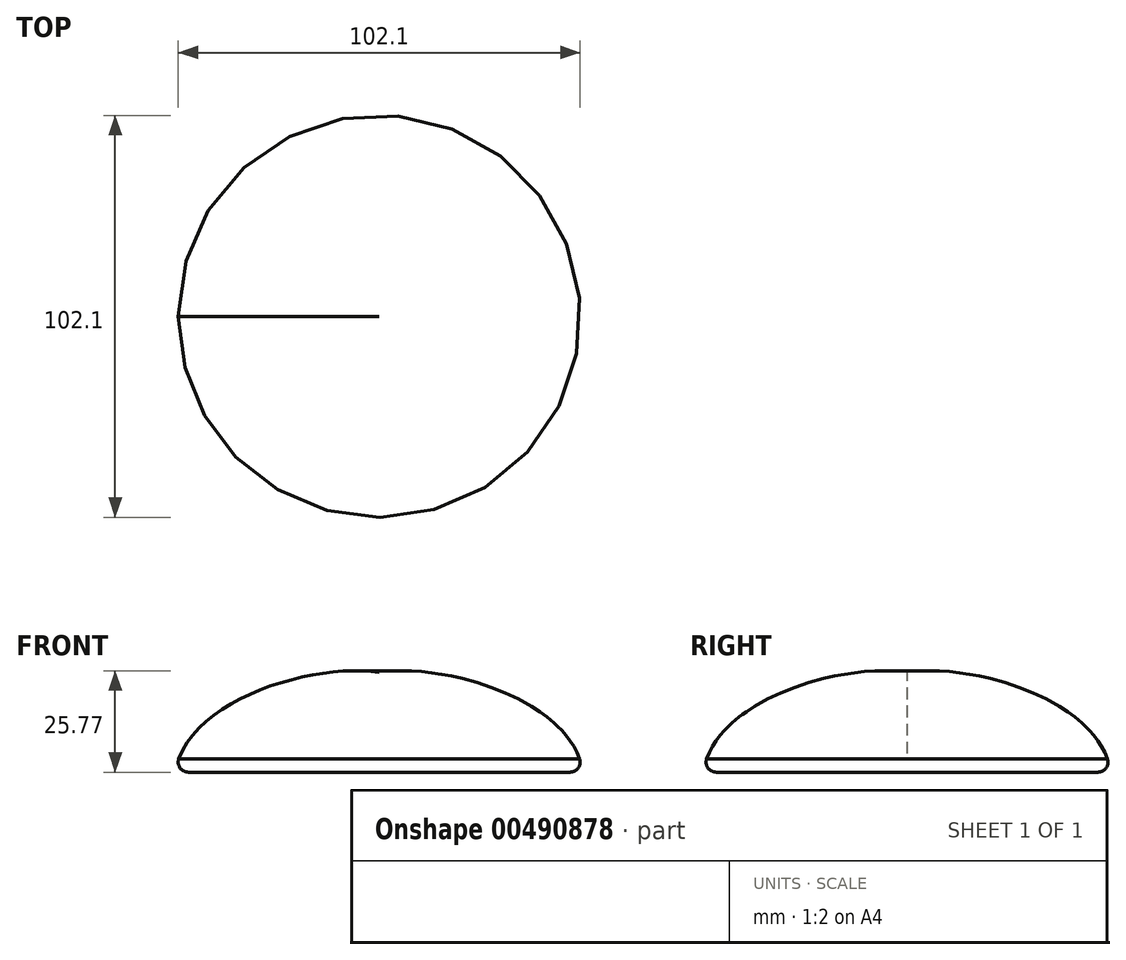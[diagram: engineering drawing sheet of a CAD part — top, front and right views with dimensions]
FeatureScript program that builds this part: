
annotation { "Feature Type Name" : "Feature", "Feature Type Description" : "" }
export const myFeature = defineFeature(function(context is Context, id is Id, definition is map)
    precondition{}
    {
        {
            var Q0;
            Q0=qCreatedBy(makeId("Front.planeOp"),FACE);
            var sketch = newSketch(context, id + "F0", { "sketchPlane" : qUnion([Q0])});
            skLineSegment(sketch, "E0", {"start": v(0, 25.4) * mm, "end": v(0, 0) * mm});
            skFitSpline(sketch, "E1", {"points": [v(0, 25.4) * mm, v(-51.8, 0) * mm], "startDerivative": vector(-49.56, 7.13) * mm, "endDerivative": vector(-8.85, -56.04) * mm});
            skLineSegment(sketch, "E2", {"start": v(-51.8, 0) * mm, "end": v(0, 0) * mm});
            skSolve(sketch);
        }
        {
            var Q0;
            Q0=makeQuery(id+"F0.imprint","IMPRINT",FACE,{"disambiguationData":[TD([[makeQuery(id+"F0.imprint","IMPRINT",EDGE,{"derivedFrom":sQuery(id+"F0.wireOp",EDGE,"E0")}),-1.0]])]});
            var Q1;
            Q1=sQuery(id+"F0.wireOp",EDGE,"E0");
            revolve(context, id + "F1", {"entities" : qUnion([Q0]), "axis" : qUnion([Q1]), "revolveType" : RevolveType.FULL});
        }
        {
            var Q0;
            Q0=makeQuery(id+"F1.opRevolve","SWEPT_FACE",FACE,{"disambiguationData":[OSD([sQuery(id+"F0.wireOp",EDGE,"E1")])]});
            var Q1;
            Q1=makeQuery(id+"F1.opRevolve","SWEPT_EDGE",EDGE,{"disambiguationData":[OSD([sQuery(id+"F0.wireOp",EDGE,"E1"),sQuery(id+"F0.wireOp",EDGE,"E2")])]});
            fillet(context, id + "F2", {"entities" : qUnion([Q0, Q1]), "radius" : 2.54 * mm, "tangentPropagation" : true, "allowEdgeOverflow" : false});
        }
    });
